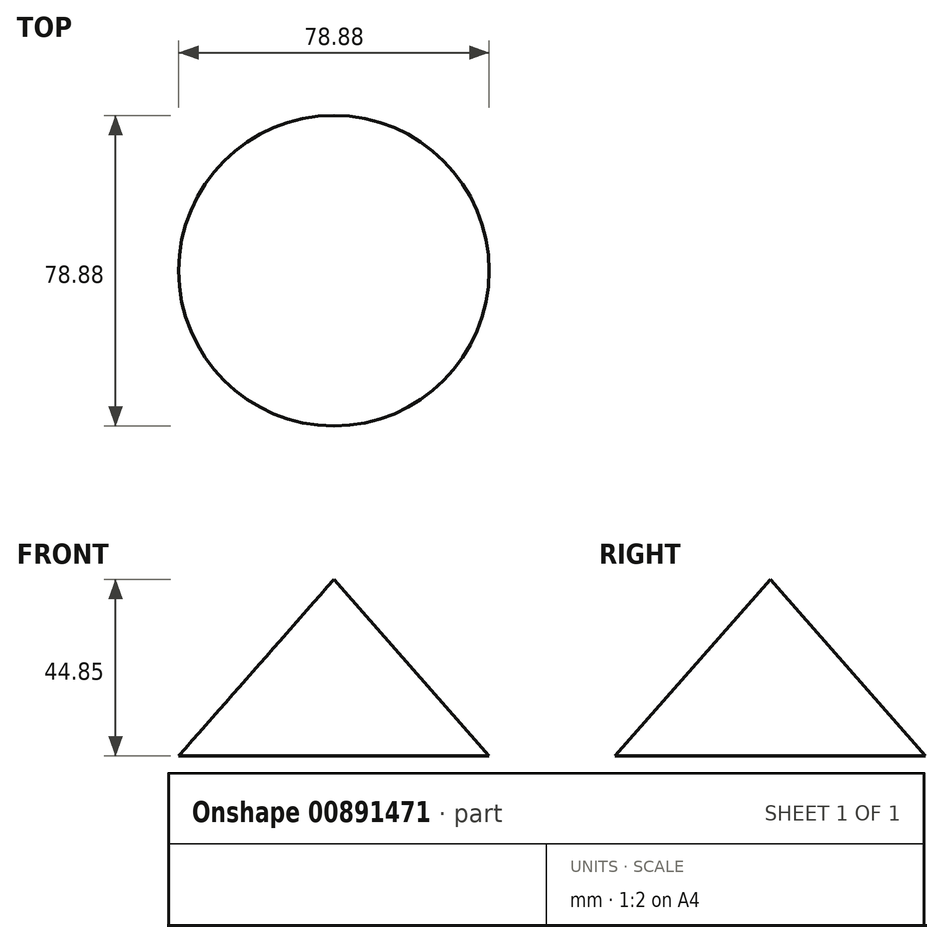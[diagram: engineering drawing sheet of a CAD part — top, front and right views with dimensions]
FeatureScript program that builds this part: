
annotation { "Feature Type Name" : "Feature", "Feature Type Description" : "" }
export const myFeature = defineFeature(function(context is Context, id is Id, definition is map)
    precondition{}
    {
        {
            var Q0;
            Q0=qCreatedBy(makeId("Front.planeOp"),FACE);
            var sketch = newSketch(context, id + "F0", { "sketchPlane" : qUnion([Q0])});
            skLineSegment(sketch, "E0", {"start": v(-39.44, 0) * mm, "end": v(0, 44.85) * mm});
            skLineSegment(sketch, "E1", {"start": v(0.31, 45.35) * mm, "end": v(0, 0) * mm});
            skLineSegment(sketch, "E2", {"start": v(-39.44, 0) * mm, "end": v(0, 0) * mm});
            skLineSegment(sketch, "E3", {"start": v(0, 0) * mm, "end": v(0, 44.85) * mm});
            skLineSegment(sketch, "E4", {"start": v(0.31, 45.35) * mm, "end": v(-39.44, 0) * mm});
            skLineSegment(sketch, "E5", {"start": v(0, 58.69) * mm, "end": v(0, -12.52) * mm});
            skSolve(sketch);
        }
        {
            var Q0;
            Q0=makeQuery(id+"F0.imprint","IMPRINT",FACE,{"disambiguationData":[TD([[makeQuery(id+"F0.imprint","IMPRINT",EDGE,{"derivedFrom":sQuery(id+"F0.wireOp",EDGE,"E0")}),-1.0]])]});
            var Q1;
            Q1=sQuery(id+"F0.wireOp",EDGE,"E5");
            revolve(context, id + "F1", {"surfaceOperationType" : NewSurfaceOperationType.NEW, "entities" : qUnion([Q0]), "axis" : qUnion([Q1]), "revolveType" : RevolveType.ONE_DIRECTION, "angle" : 360 * degree});
        }
    });
